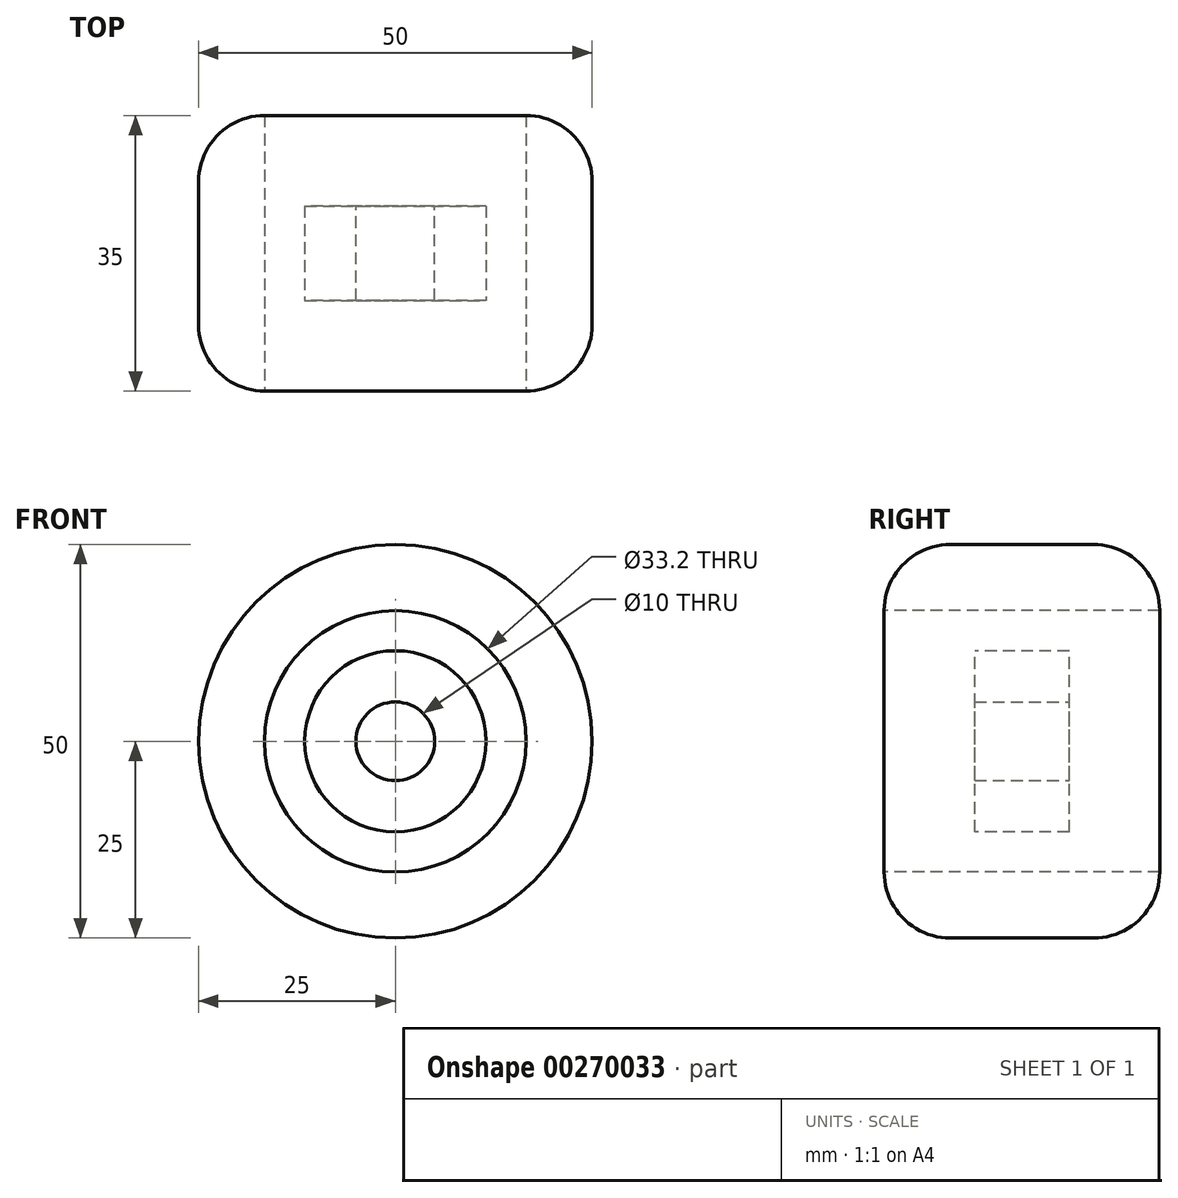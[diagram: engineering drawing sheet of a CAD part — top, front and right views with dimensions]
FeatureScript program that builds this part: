
annotation { "Feature Type Name" : "Feature", "Feature Type Description" : "" }
export const myFeature = defineFeature(function(context is Context, id is Id, definition is map)
    precondition{}
    {
        {
            var Q0;
            Q0=qCreatedBy(makeId("Front.planeOp"),FACE);
            var sketch = newSketch(context, id + "F0", { "sketchPlane" : qUnion([Q0])});
            skCircle(sketch, "E0", {"center": v(0, 0) * mm, "radius": 25 * mm});
            skCircle(sketch, "E1", {"center": v(0, 0) * mm, "radius": 5 * mm});
            skCircle(sketch, "E2", {"center": v(0, 0) * mm, "radius": 11.5 * mm});
            skSolve(sketch);
        }
        {
            var Q0;
            Q0=makeQuery(id+"F0.imprint","IMPRINT",FACE,{"disambiguationData":[TD([[makeQuery(id+"F0.imprint","IMPRINT",EDGE,{"derivedFrom":sQuery(id+"F0.wireOp",EDGE,"E0")}),1.0]])]});
            extrude(context, id + "F1", {"entities" : qUnion([Q0]), "depth" : 17.5 * mm, "offsetDistance" : 25 * mm, "hasSecondDirection" : true, "secondDirectionOppositeDirection" : true, "secondDirectionDepth" : 17.5 * mm});
        }
        {
            var Q0;
            Q0=makeQuery(id+"F0.imprint","IMPRINT",FACE,{"disambiguationData":[TD([[makeQuery(id+"F0.imprint","IMPRINT",EDGE,{"derivedFrom":sQuery(id+"F0.wireOp",EDGE,"E1")}),-1.0]])]});
            extrude(context, id + "F2", {"entities" : qUnion([Q0]), "operationType" : NewBodyOperationType.ADD, "depth" : 6 * mm, "offsetDistance" : 25 * mm});
        }
        {
            var Q0;
            Q0=makeQuery(id+"F0.imprint","IMPRINT",FACE,{"disambiguationData":[TD([[makeQuery(id+"F0.imprint","IMPRINT",EDGE,{"derivedFrom":sQuery(id+"F0.wireOp",EDGE,"E1")}),-1.0]])]});
            extrude(context, id + "F3", {"entities" : qUnion([Q0]), "operationType" : NewBodyOperationType.ADD, "oppositeDirection" : true, "depth" : 6 * mm, "offsetDistance" : 25 * mm});
        }
        {
            var Q0;
            Q0=makeQuery(id+"F1.opExtrude","CAP_EDGE",EDGE,{"disambiguationData":[OSD([sQuery(id+"F0.wireOp",EDGE,"E0")])],"isStart":false});
            var Q1;
            Q1=makeQuery(id+"F1.opExtrude","CAP_EDGE",EDGE,{"disambiguationData":[OSD([sQuery(id+"F0.wireOp",EDGE,"E0")])],"isStart":true});
            fillet(context, id + "F4", {"entities" : qUnion([Q0, Q1]), "radius" : 8.4 * mm, "tangentPropagation" : true, "allowEdgeOverflow" : false});
        }
        {
            var Q0;
            Q0=qCreatedBy(makeId("Top.planeOp"),FACE);
            var sketch = newSketch(context, id + "F5", { "sketchPlane" : qUnion([Q0])});
            skLineSegment(sketch, "E3.0", {"start": v(11.5, 0) * mm, "end": v(-11.5, 0) * mm});
            skLineSegment(sketch, "E4", {"start": v(25, 9.53) * mm, "end": v(25, -9.53) * mm});
            skLineSegment(sketch, "E5", {"start": v(-25, -9.53) * mm, "end": v(-25, 9.53) * mm});
            skSolve(sketch);
        }
        {
            var Q0;
            Q0=makeQuery(id+"F1.opExtrude","CAP_FACE",FACE,{"disambiguationData":[OSD([sQuery(id+"F0.wireOp",EDGE,"E0"),sQuery(id+"F0.wireOp",EDGE,"E2")])],"isStart":false});
            extrude(context, id + "F6", {"entities" : qUnion([Q0]), "operationType" : NewBodyOperationType.REMOVE, "oppositeDirection" : true, "depth" : 110.7 * mm, "offsetDistance" : 25 * mm});
        }
    });
